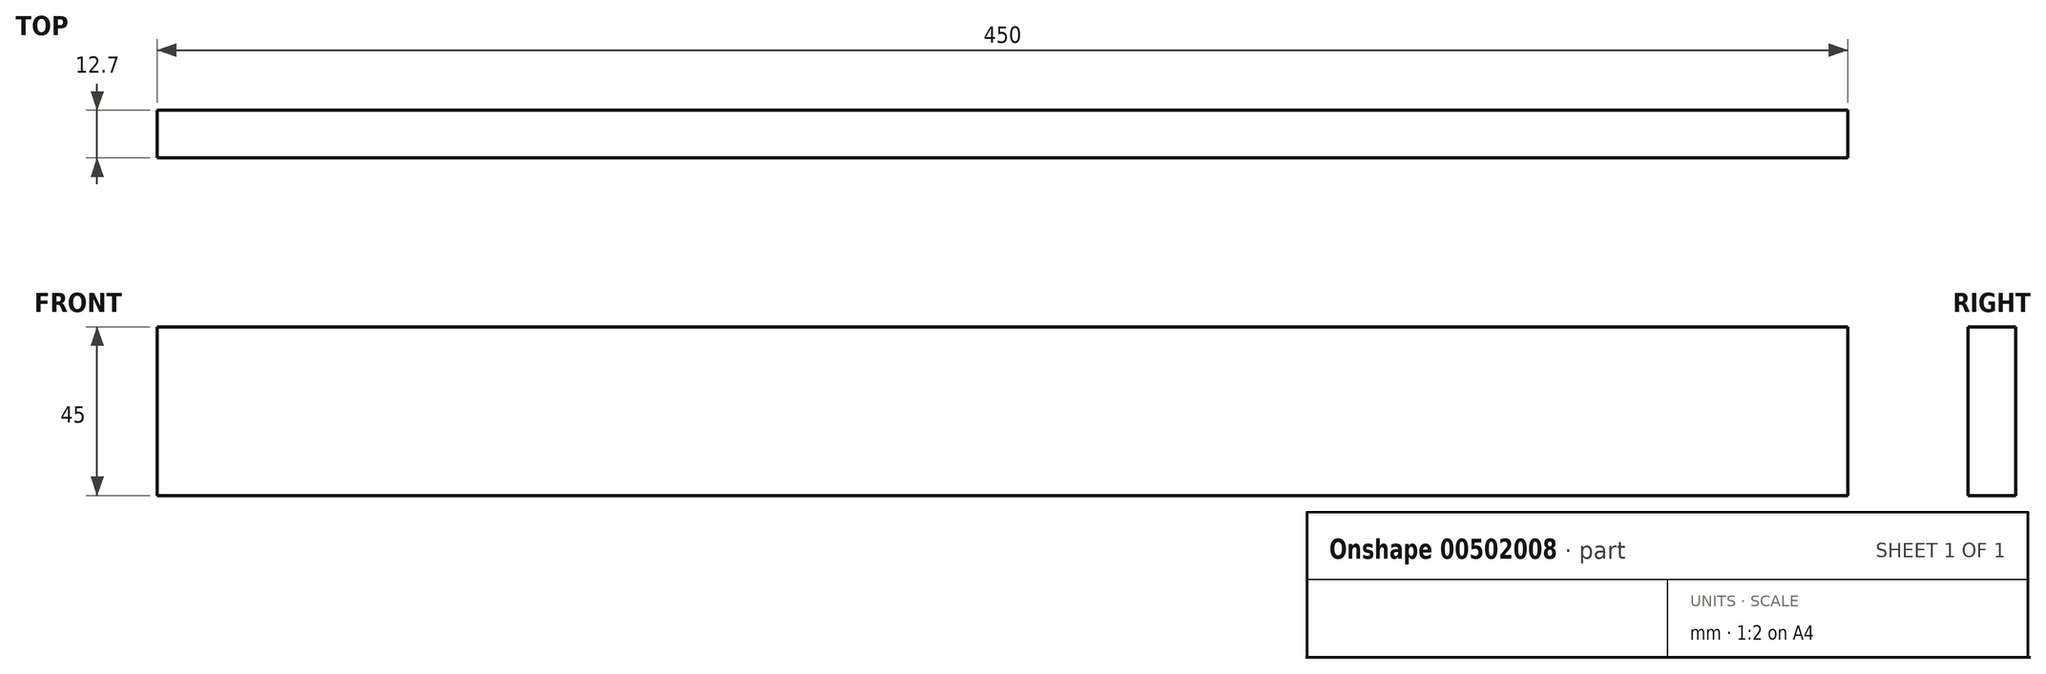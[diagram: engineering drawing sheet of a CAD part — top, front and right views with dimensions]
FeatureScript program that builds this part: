
annotation { "Feature Type Name" : "Feature", "Feature Type Description" : "" }
export const myFeature = defineFeature(function(context is Context, id is Id, definition is map)
    precondition{}
    {
        {
            var Q0;
            Q0=qCreatedBy(makeId("Front.planeOp"),FACE);
            var sketch = newSketch(context, id + "F0", { "sketchPlane" : qUnion([Q0])});
            skLineSegment(sketch, "E0.bottom", {"start": v(0, 0) * mm, "end": v(450, 0) * mm});
            skLineSegment(sketch, "E0.top", {"start": v(0, 45) * mm, "end": v(450, 45) * mm});
            skLineSegment(sketch, "E0.left", {"start": v(0, 0) * mm, "end": v(0, 45) * mm});
            skLineSegment(sketch, "E0.right", {"start": v(450, 0) * mm, "end": v(450, 45) * mm});
            skSolve(sketch);
        }
        {
            var Q0;
            Q0=makeQuery(id+"F0.imprint","IMPRINT",FACE,{"disambiguationData":[TD([[makeQuery(id+"F0.imprint","IMPRINT",EDGE,{"derivedFrom":sQuery(id+"F0.wireOp",EDGE,"E0.bottom")}),1.0]])]});
            extrude(context, id + "F1", {"entities" : qUnion([Q0]), "depth" : 12.7 * mm});
        }
    });
